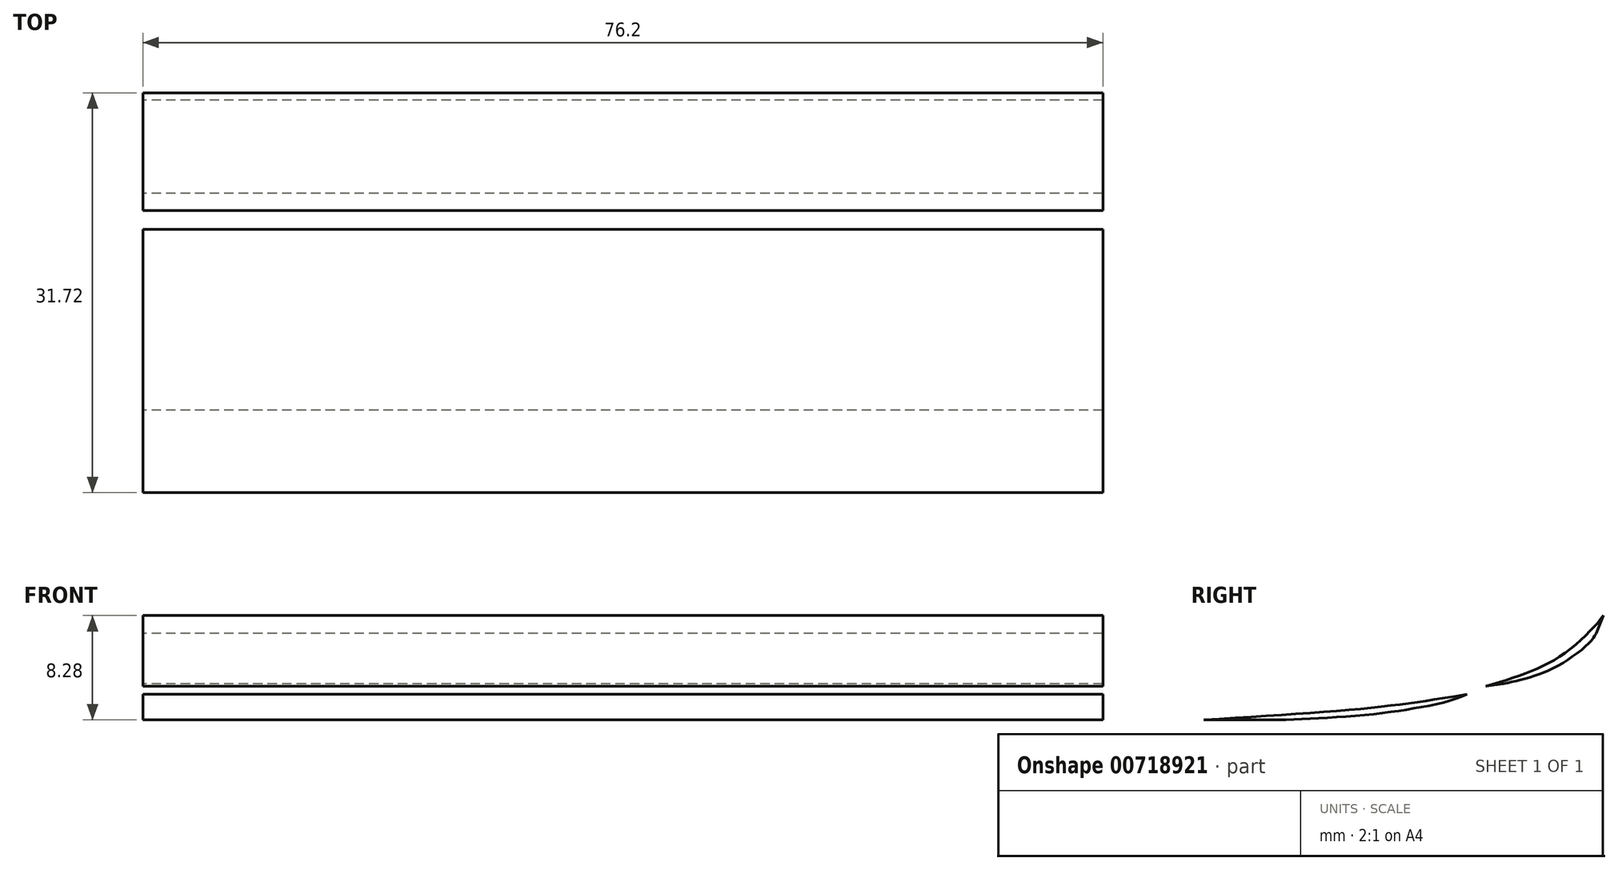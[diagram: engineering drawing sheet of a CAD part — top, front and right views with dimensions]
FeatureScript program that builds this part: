
annotation { "Feature Type Name" : "Feature", "Feature Type Description" : "" }
export const myFeature = defineFeature(function(context is Context, id is Id, definition is map)
    precondition{}
    {
        {
            var Q0;
            Q0=qCreatedBy(makeId("Right.planeOp"),FACE);
            var sketch = newSketch(context, id + "F0", { "sketchPlane" : qUnion([Q0])});
            skFitSpline(sketch, "E0", {"points": [v(-20.9, 0) * mm, v(-9.14, 0.8) * mm, v(-3.87, 1.42) * mm, v(0, 2.03) * mm], "startDerivative": vector(28.98, 1.77) * mm, "endDerivative": vector(14.9, 2.45) * mm});
            skLineSegment(sketch, "E1", {"start": v(-20.9, 0) * mm, "end": v(-14.36, 0) * mm});
            skFitSpline(sketch, "E2", {"points": [v(-14.36, 0) * mm, v(-11.16, 0.15) * mm, v(-7.19, 0.48) * mm, v(-4.2, 0.9) * mm, v(-1.67, 1.43) * mm, v(0, 2.03) * mm], "startDerivative": vector(14.53, 0.6) * mm, "endDerivative": vector(10.01, 3.97) * mm});
            skSolve(sketch);
        }
        {
            var Q0;
            Q0=qCreatedBy(makeId("Right.planeOp"),FACE);
            var sketch = newSketch(context, id + "F1", { "sketchPlane" : qUnion([Q0])});
            skFitSpline(sketch, "E3", {"points": [v(1.51, 2.66) * mm, v(5.05, 3.84) * mm, v(7.83, 5.34) * mm, v(10.18, 7.48) * mm, v(10.83, 8.28) * mm], "startDerivative": vector(12.38, 3.79) * mm, "endDerivative": vector(3.3, 4.52) * mm});
            skLineSegment(sketch, "E4", {"start": v(1.51, 2.66) * mm, "end": v(2.88, 2.86) * mm});
            skFitSpline(sketch, "E5", {"points": [v(2.88, 2.86) * mm, v(4.9, 3.35) * mm, v(7.31, 4.34) * mm, v(9.7, 6.1) * mm, v(10.26, 6.86) * mm], "startDerivative": vector(8, 1.75) * mm, "endDerivative": vector(2.44, 4.14) * mm});
            skLineSegment(sketch, "E6", {"start": v(10.26, 6.86) * mm, "end": v(10.83, 8.28) * mm});
            skSolve(sketch);
        }
        {
            var Q0;
            Q0 = qSketchRegion(id + "F0", true);
            extrude(context, id + "F2", {"entities" : qUnion([Q0]), "depth" : 76.2 * mm, "offsetDistance" : 25.4 * mm});
        }
        {
            var Q0;
            Q0 = qSketchRegion(id + "F1", true);
            extrude(context, id + "F3", {"entities" : qUnion([Q0]), "depth" : 76.2 * mm, "offsetDistance" : 25.4 * mm});
        }
    });
